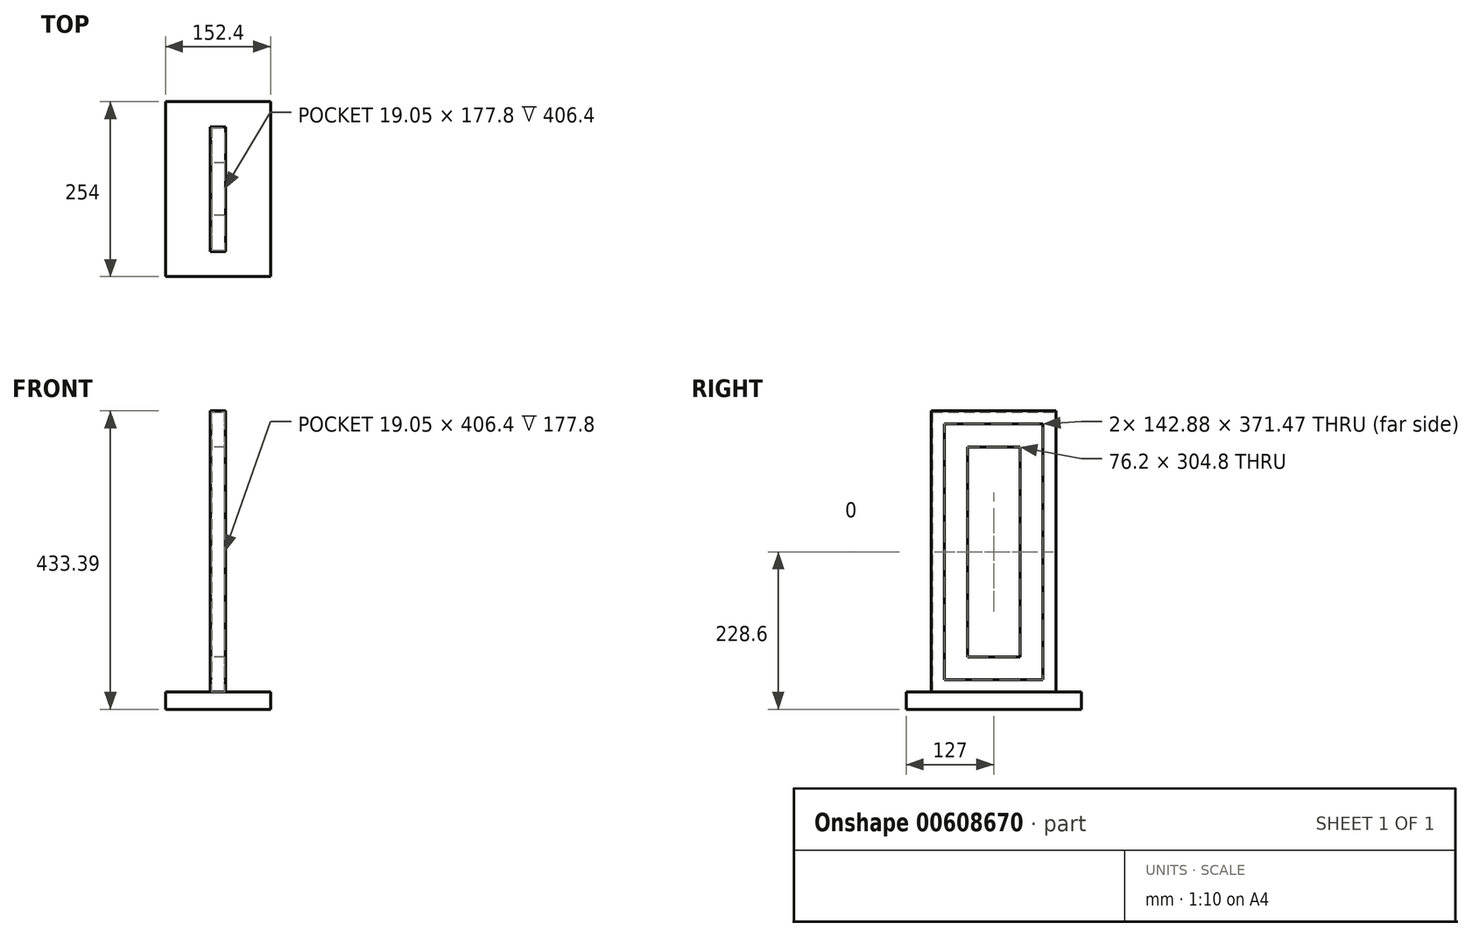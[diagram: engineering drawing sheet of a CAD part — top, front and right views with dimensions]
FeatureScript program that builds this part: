
annotation { "Feature Type Name" : "Feature", "Feature Type Description" : "" }
export const myFeature = defineFeature(function(context is Context, id is Id, definition is map)
    precondition{}
    {
        {
            var Q0;
            Q0=qCreatedBy(makeId("Right.planeOp"),FACE);
            var sketch = newSketch(context, id + "F0", { "sketchPlane" : qUnion([Q0])});
            skLineSegment(sketch, "E0.bottom", {"start": v(38.1, 76.2) * mm, "end": v(-38.1, 76.2) * mm});
            skLineSegment(sketch, "E0.top", {"start": v(38.1, 381) * mm, "end": v(-38.1, 381) * mm});
            skLineSegment(sketch, "E0.left", {"start": v(38.1, 76.2) * mm, "end": v(38.1, 381) * mm});
            skLineSegment(sketch, "E0.right", {"start": v(-38.1, 76.2) * mm, "end": v(-38.1, 381) * mm});
            skPoint(sketch, "E0.middle", {"position": v(0, 228.6) * mm});
            skLineSegment(sketch, "E1.bottom", {"start": v(88.9, 25.4) * mm, "end": v(-88.9, 25.4) * mm});
            skLineSegment(sketch, "E1.top", {"start": v(88.9, 431.8) * mm, "end": v(-88.9, 431.8) * mm});
            skLineSegment(sketch, "E1.left", {"start": v(88.9, 25.4) * mm, "end": v(88.9, 431.8) * mm});
            skLineSegment(sketch, "E1.right", {"start": v(-88.9, 25.4) * mm, "end": v(-88.9, 431.8) * mm});
            skLineSegment(sketch, "E2.bottom", {"start": v(-127, 0) * mm, "end": v(127, 0) * mm});
            skLineSegment(sketch, "E2.top", {"start": v(-127, 25.4) * mm, "end": v(127, 25.4) * mm});
            skLineSegment(sketch, "E2.left", {"start": v(-127, 0) * mm, "end": v(-127, 25.4) * mm});
            skLineSegment(sketch, "E2.right", {"start": v(127, 0) * mm, "end": v(127, 25.4) * mm});
            skPoint(sketch, "E2.middle", {"position": v(0, 12.7) * mm});
            skSolve(sketch);
        }
        {
            var Q0;
            Q0=makeQuery(id+"F0.imprint","IMPRINT",FACE,{"disambiguationData":[TD([[makeQuery(id+"F0.imprint","IMPRINT",EDGE,{"derivedFrom":sQuery(id+"F0.wireOp",EDGE,"E0.bottom")}),1.0]])]});
            extrude(context, id + "F1", {"entities" : qUnion([Q0]), "endBound" : BoundingType.SYMMETRIC, "depth" : 19.05 * mm, "offsetDistance" : 25.4 * mm});
        }
        {
            var Q0;
            Q0=makeQuery(id+"F0.imprint","IMPRINT",FACE,{"disambiguationData":[TD([[makeQuery(id+"F0.imprint","IMPRINT",EDGE,{"derivedFrom":sQuery(id+"F0.wireOp",EDGE,"E2.bottom")}),1.0]])]});
            extrude(context, id + "F2", {"entities" : qUnion([Q0]), "endBound" : BoundingType.SYMMETRIC, "depth" : 152.4 * mm, "offsetDistance" : 25.4 * mm});
        }
        {
            var Q0;
            Q0=makeQuery(id+"F2.opExtrude","SWEPT_FACE",FACE,{"disambiguationData":[OSD([sQuery(id+"F0.wireOp",EDGE,"E2.top")])]});
            var sketch = newSketch(context, id + "F3", { "sketchPlane" : qUnion([Q0])});
            skLineSegment(sketch, "E3.0.0", {"start": v(-9.53, 88.9) * mm, "end": v(-9.53, -88.9) * mm, "construction": true});
            skLineSegment(sketch, "E3.0.1", {"start": v(-9.52, -88.9) * mm, "end": v(9.53, -88.9) * mm, "construction": true});
            skLineSegment(sketch, "E3.0.2", {"start": v(9.53, -88.9) * mm, "end": v(9.53, 88.9) * mm, "construction": true});
            skLineSegment(sketch, "E3.0.3", {"start": v(9.53, 88.9) * mm, "end": v(-9.52, 88.9) * mm, "construction": true});
            skLineSegment(sketch, "E4", {"start": v(-9.52, -88.9) * mm, "end": v(-9.53, -71.44) * mm});
            skLineSegment(sketch, "E5", {"start": v(-9.52, -71.44) * mm, "end": v(-11.11, -71.44) * mm});
            skLineSegment(sketch, "E6", {"start": v(-11.11, -71.44) * mm, "end": v(-11.11, -90.49) * mm});
            skLineSegment(sketch, "E7", {"start": v(-11.11, -90.49) * mm, "end": v(11.11, -90.49) * mm});
            skLineSegment(sketch, "E8", {"start": v(11.11, -90.49) * mm, "end": v(11.11, -71.44) * mm});
            skLineSegment(sketch, "E9", {"start": v(11.11, -71.44) * mm, "end": v(9.52, -71.44) * mm});
            skLineSegment(sketch, "E10", {"start": v(9.53, -71.44) * mm, "end": v(9.53, -88.9) * mm});
            skLineSegment(sketch, "E11", {"start": v(9.53, -88.9) * mm, "end": v(9.53, 88.9) * mm});
            skLineSegment(sketch, "E12", {"start": v(-9.53, -88.9) * mm, "end": v(9.53, -88.9) * mm});
            skSolve(sketch);
        }
        {
            var Q0;
            Q0=makeQuery(id+"F3.imprint","IMPRINT",FACE,{"disambiguationData":[TD([[makeQuery(id+"F3.imprint","IMPRINT",EDGE,{"derivedFrom":sQuery(id+"F3.wireOp",EDGE,"E4")}),1.0]])]});
            var Q1;
            Q1=makeQuery(id+"F1.opExtrude","CAP_EDGE",EDGE,{"disambiguationData":[OSD([sQuery(id+"F0.wireOp",EDGE,"E1.right")])],"isStart":false});
            var Q2;
            Q2=makeQuery(id+"F1.opExtrude","CAP_EDGE",EDGE,{"disambiguationData":[OSD([sQuery(id+"F0.wireOp",EDGE,"E1.top")])],"isStart":false});
            var Q3;
            Q3=makeQuery(id+"F1.opExtrude","CAP_EDGE",EDGE,{"disambiguationData":[OSD([sQuery(id+"F0.wireOp",EDGE,"E1.left")])],"isStart":false});
            var Q4;
            Q4=sQuery(id+"F3.wireOp",EDGE,"E11");
            sweep(context, id + "F4", {"profiles" : qUnion([Q0]), "path" : qUnion([Q1, Q2, Q3, Q4])});
        }
    });
